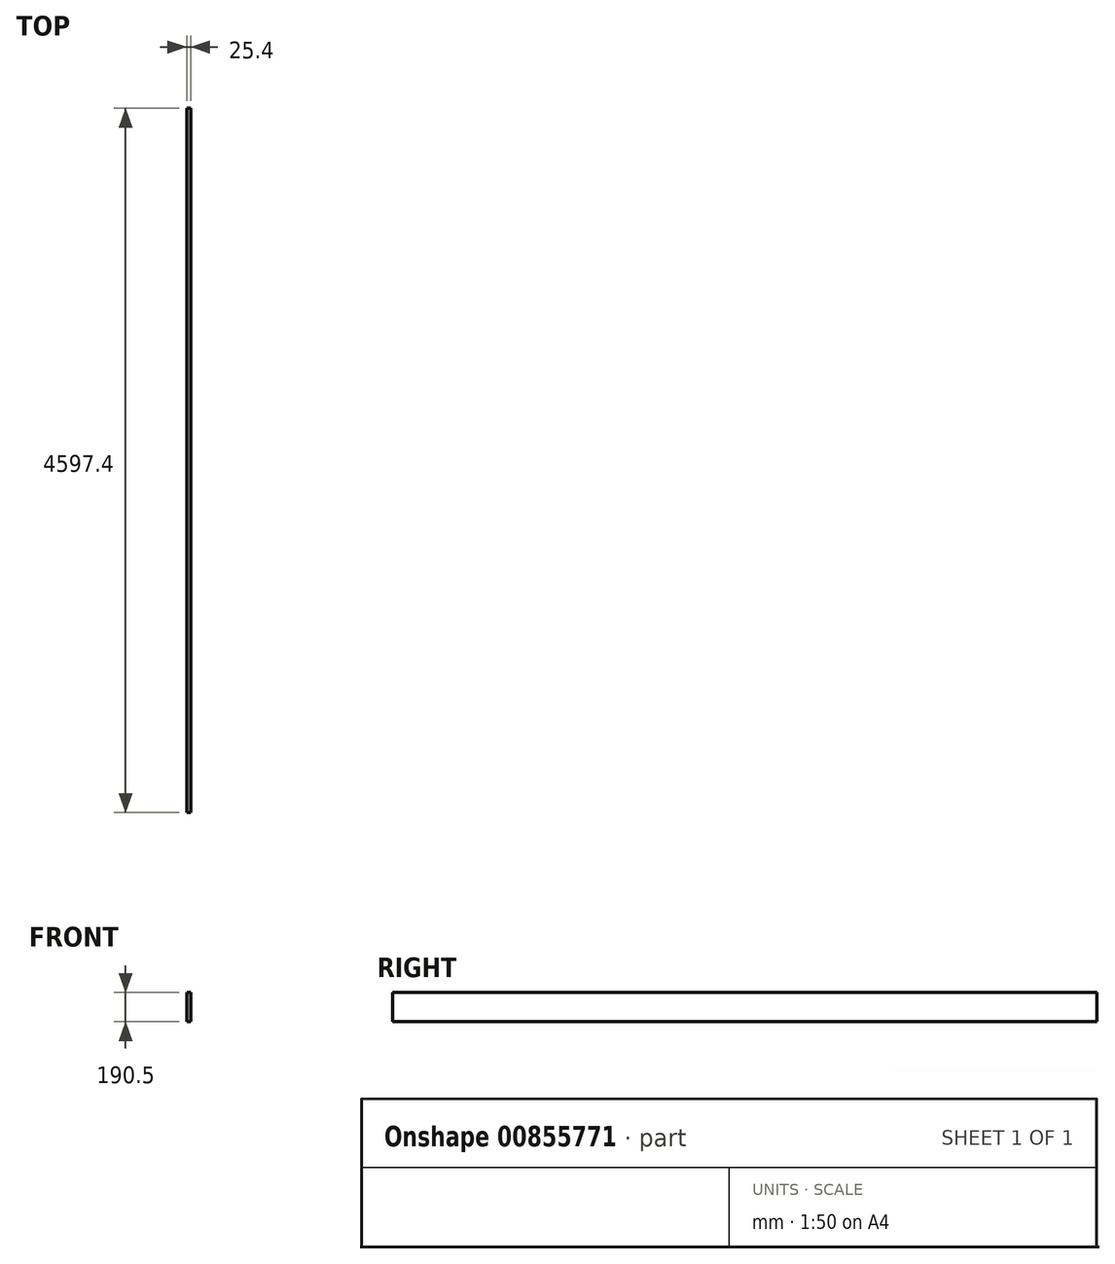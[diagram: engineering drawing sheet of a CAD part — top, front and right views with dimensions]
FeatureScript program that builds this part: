
annotation { "Feature Type Name" : "Feature", "Feature Type Description" : "" }
export const myFeature = defineFeature(function(context is Context, id is Id, definition is map)
    precondition{}
    {
        {
            var Q0;
            Q0=qCreatedBy(makeId("Front.planeOp"),FACE);
            var sketch = newSketch(context, id + "F0", { "sketchPlane" : qUnion([Q0])});
            skLineSegment(sketch, "E0.bottom", {"start": v(0, 0) * mm, "end": v(25.4, 0) * mm});
            skLineSegment(sketch, "E0.top", {"start": v(0, -190.5) * mm, "end": v(25.4, -190.5) * mm});
            skLineSegment(sketch, "E0.left", {"start": v(0, 0) * mm, "end": v(0, -190.5) * mm});
            skLineSegment(sketch, "E0.right", {"start": v(25.4, 0) * mm, "end": v(25.4, -190.5) * mm});
            skSolve(sketch);
        }
        {
            var Q0;
            Q0=makeQuery(id+"F0.imprint","IMPRINT",FACE,{"disambiguationData":[TD([[makeQuery(id+"F0.imprint","IMPRINT",EDGE,{"derivedFrom":sQuery(id+"F0.wireOp",EDGE,"E0.bottom")}),-1.0]])]});
            extrude(context, id + "F1", {"entities" : qUnion([Q0]), "oppositeDirection" : true, "depth" : 4597.4 * mm, "offsetDistance" : 25.4 * mm});
        }
    });
